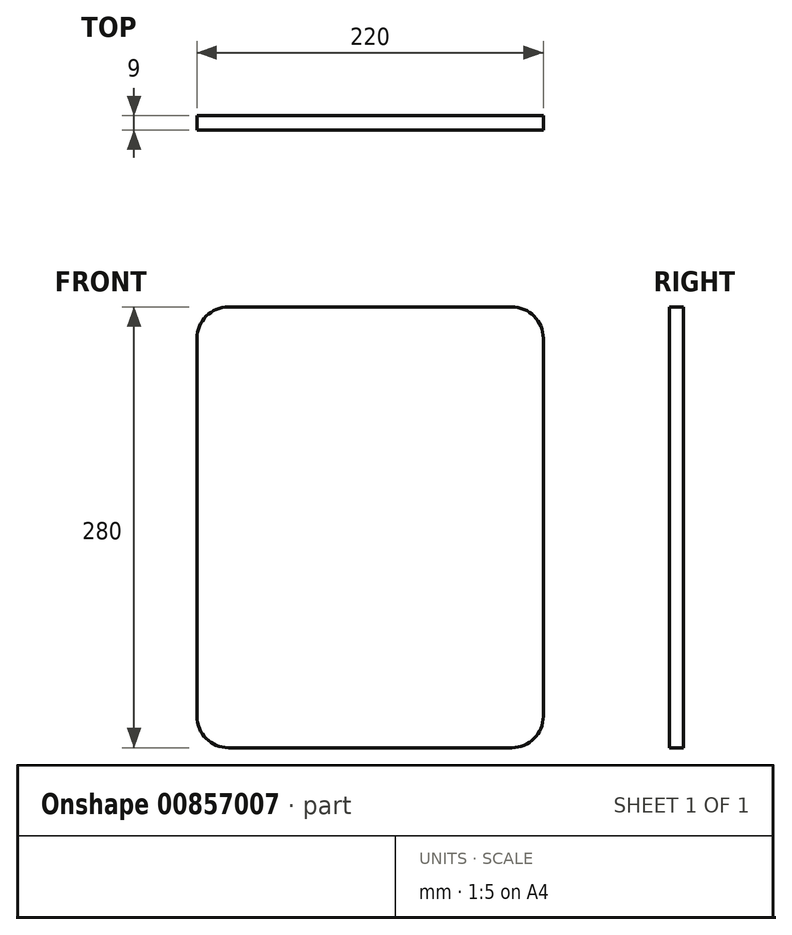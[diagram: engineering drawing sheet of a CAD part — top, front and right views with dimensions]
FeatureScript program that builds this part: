
annotation { "Feature Type Name" : "Feature", "Feature Type Description" : "" }
export const myFeature = defineFeature(function(context is Context, id is Id, definition is map)
    precondition{}
    {
        {
            var Q0;
            Q0=qCreatedBy(makeId("Front.planeOp"),FACE);
            var sketch = newSketch(context, id + "F0", { "sketchPlane" : qUnion([Q0])});
            skLineSegment(sketch, "E0.bottom", {"start": v(102.22, 153.33) * mm, "end": v(-77.78, 153.33) * mm});
            skLineSegment(sketch, "E0.top", {"start": v(102.22, -126.67) * mm, "end": v(-77.78, -126.67) * mm});
            skLineSegment(sketch, "E0.left", {"start": v(122.22, 133.33) * mm, "end": v(122.22, -106.67) * mm});
            skLineSegment(sketch, "E0.right", {"start": v(-97.78, -106.65) * mm, "end": v(-97.78, -106.67) * mm});
            skArc(sketch, "E1.filletArc", {"start": v(-77.78, 153.33) * mm, "mid": v(-91.92, 147.47) * mm, "end": v(-97.78, 133.33) * mm});
            skArc(sketch, "E2.filletArc", {"start": v(122.22, 133.33) * mm, "mid": v(116.36, 147.47) * mm, "end": v(102.22, 153.33) * mm});
            skArc(sketch, "E3.filletArc", {"start": v(102.22, -126.67) * mm, "mid": v(116.36, -120.81) * mm, "end": v(122.22, -106.67) * mm});
            skArc(sketch, "E4.filletArc", {"start": v(-97.78, -106.67) * mm, "mid": v(-91.92, -120.81) * mm, "end": v(-77.78, -126.67) * mm});
            skLineSegment(sketch, "E5", {"start": v(-97.78, -106.65) * mm, "end": v(-97.78, 133.33) * mm});
            skSolve(sketch);
        }
        {
            var Q0;
            Q0=makeQuery(id+"F0.imprint","IMPRINT",FACE,{"disambiguationData":[TD([[makeQuery(id+"F0.imprint","IMPRINT",EDGE,{"derivedFrom":sQuery(id+"F0.wireOp",EDGE,"E0.bottom")}),1.0]])]});
            extrude(context, id + "F1", {"entities" : qUnion([Q0]), "oppositeDirection" : true, "depth" : 9 * mm, "offsetDistance" : 25 * mm});
        }
    });
